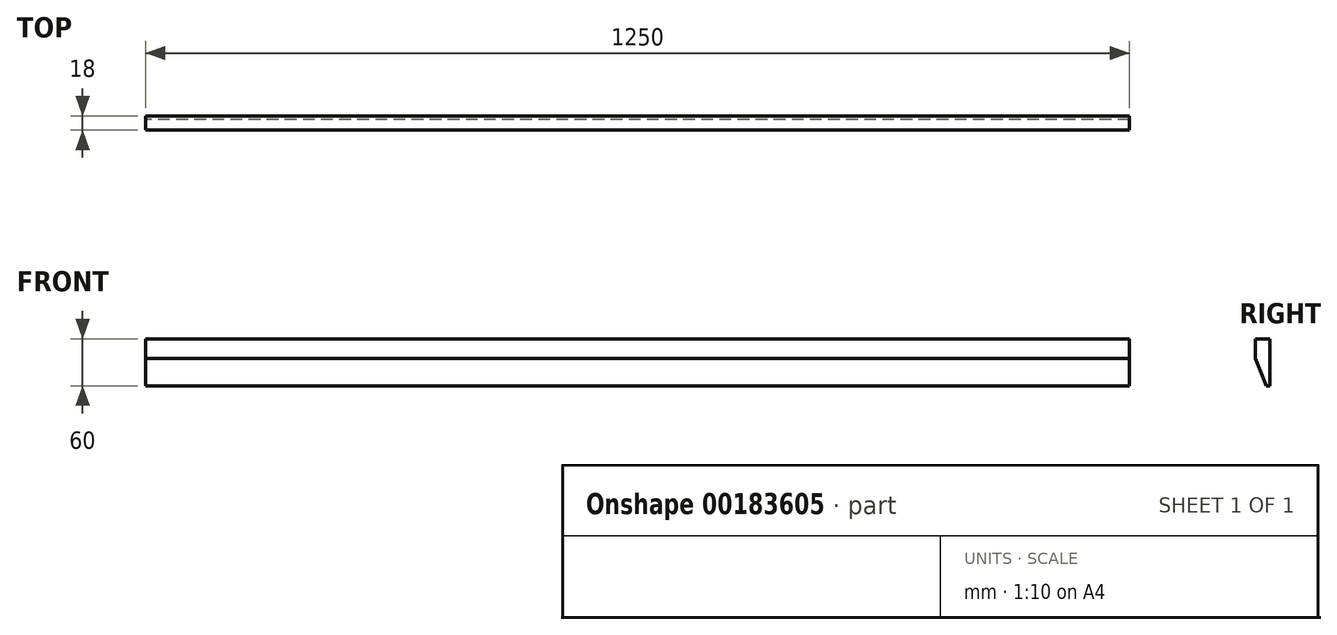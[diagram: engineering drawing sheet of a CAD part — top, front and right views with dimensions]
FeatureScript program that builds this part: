
annotation { "Feature Type Name" : "Feature", "Feature Type Description" : "" }
export const myFeature = defineFeature(function(context is Context, id is Id, definition is map)
    precondition{}
    {
        {
            var Q0;
            Q0=qCreatedBy(makeId("Right.planeOp"),FACE);
            var sketch = newSketch(context, id + "F0", { "sketchPlane" : qUnion([Q0])});
            skLineSegment(sketch, "E0.bottom", {"start": v(9, 30) * mm, "end": v(-9, 30) * mm});
            skLineSegment(sketch, "E0.top", {"start": v(9, -30) * mm, "end": v(4.7, -30) * mm});
            skLineSegment(sketch, "E0.left", {"start": v(9, 30) * mm, "end": v(9, -30) * mm});
            skLineSegment(sketch, "E0.right", {"start": v(-9, 30) * mm, "end": v(-9, 5) * mm});
            skPoint(sketch, "E0.middle", {"position": v(0, 0) * mm});
            skLineSegment(sketch, "E1", {"start": v(4.7, -30) * mm, "end": v(-9, 5) * mm});
            skPoint(sketch, "E2.orphan", {"position": v(-9, -30) * mm});
            skSolve(sketch);
        }
        {
            var Q0;
            Q0 = qSketchRegion(id + "F0", true);
            extrude(context, id + "F1", {"entities" : qUnion([Q0]), "depth" : 1250 * mm});
        }
    });
